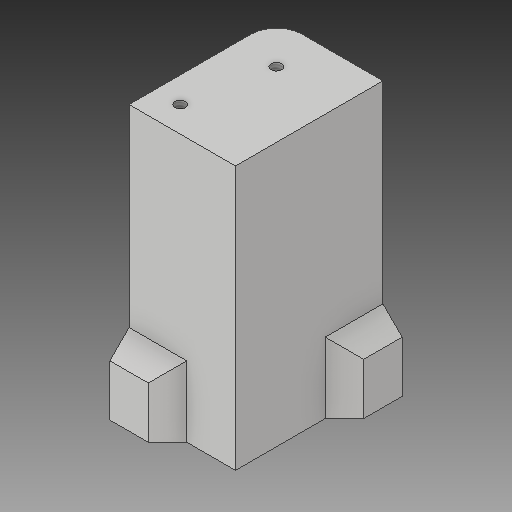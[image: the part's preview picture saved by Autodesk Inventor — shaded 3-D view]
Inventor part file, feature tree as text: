
AUTODESK INVENTOR PART (.ipt)
format: ipt  version: 2017 (Build 210142000, 142)  size: 193,536 bytes
history: native  units: in
note: dims shown in document units (in); Inventor stores cm internally (conversion verified against a paired STEP export)
features: sketch x6, projected_geometry x5, extrude x4, fillet x2, hole x2, chamfer x1
ambient origin geometry x8: Origin, YZ Plane, XZ Plane, XY Plane, X Axis, Y Axis, Z Axis, Center Point
bodies: Solid1 (feature_tree)
feature tree (20):
  extrude  "Extrusion1"  Depth=0.636in
  extrude  "Extrusion3"  Depth=1.4375in
  extrude  "Extrusion4"  Depth=0.1875in TaperAngle=0.0deg
  fillet  "Fillet1"  Radius=1.25in
  extrude  "Extrusion5"  Depth=0.85in TaperAngle=0.0deg
  chamfer  "Chamfer1"  Distance=0.375in
  hole  "Hole1"  [1 undecoded]
  hole  "Hole2"  [1 undecoded]
  fillet  "Fillet2"  Radius=0.5in
  sketch  "Sketch1"  dims[d0=2.57in d1=0.636in]
  sketch  "Sketch3"  dims[d4=0.1875in d5=0.0in d11=1.4375in]
  projected_geometry  "Projected Loop2"
  sketch  "Sketch4"  dims[d12=1.0375in d13=0.1875in d14=0.0in d15=1.25in]
  projected_geometry  "Projected Loop3"
  sketch  "Sketch6"  dims[d16=0.85in d17=0.1875in d18=0.0in]
  projected_geometry  "Projected Loop5"
  sketch  "Sketch8"  dims[d19=0.0625in]
  projected_geometry  "Projected Loop6"
  sketch  "Sketch9"  dims[d24=0.375in d25=0.375in d26=0.375in d27=0.375in d28=0.5in d29=0.0in d30=0.1875in d31=0.125in d32=45.0deg d33=0.104in d34=0.276in d35=0.375in d36=0.25in d37=0.5635in d38=0.5in d39=0.8108in d41=0.104in d42=0.276in d43=0.375in d44=0.25in d45=0.5635in d46=0.432in d47=0.8108in d50=1.25in d51=0.85in d52=0.25in d56=0.4in d57=0.25in d58=0.4in d59=0.25in]
  projected_geometry  "Projected Loop7"
note: 2 required parameter values undecoded (feature->parameter linkage not recoverable at this tier; creation-order binding heuristic only, values carry confidence <= 0.55)
